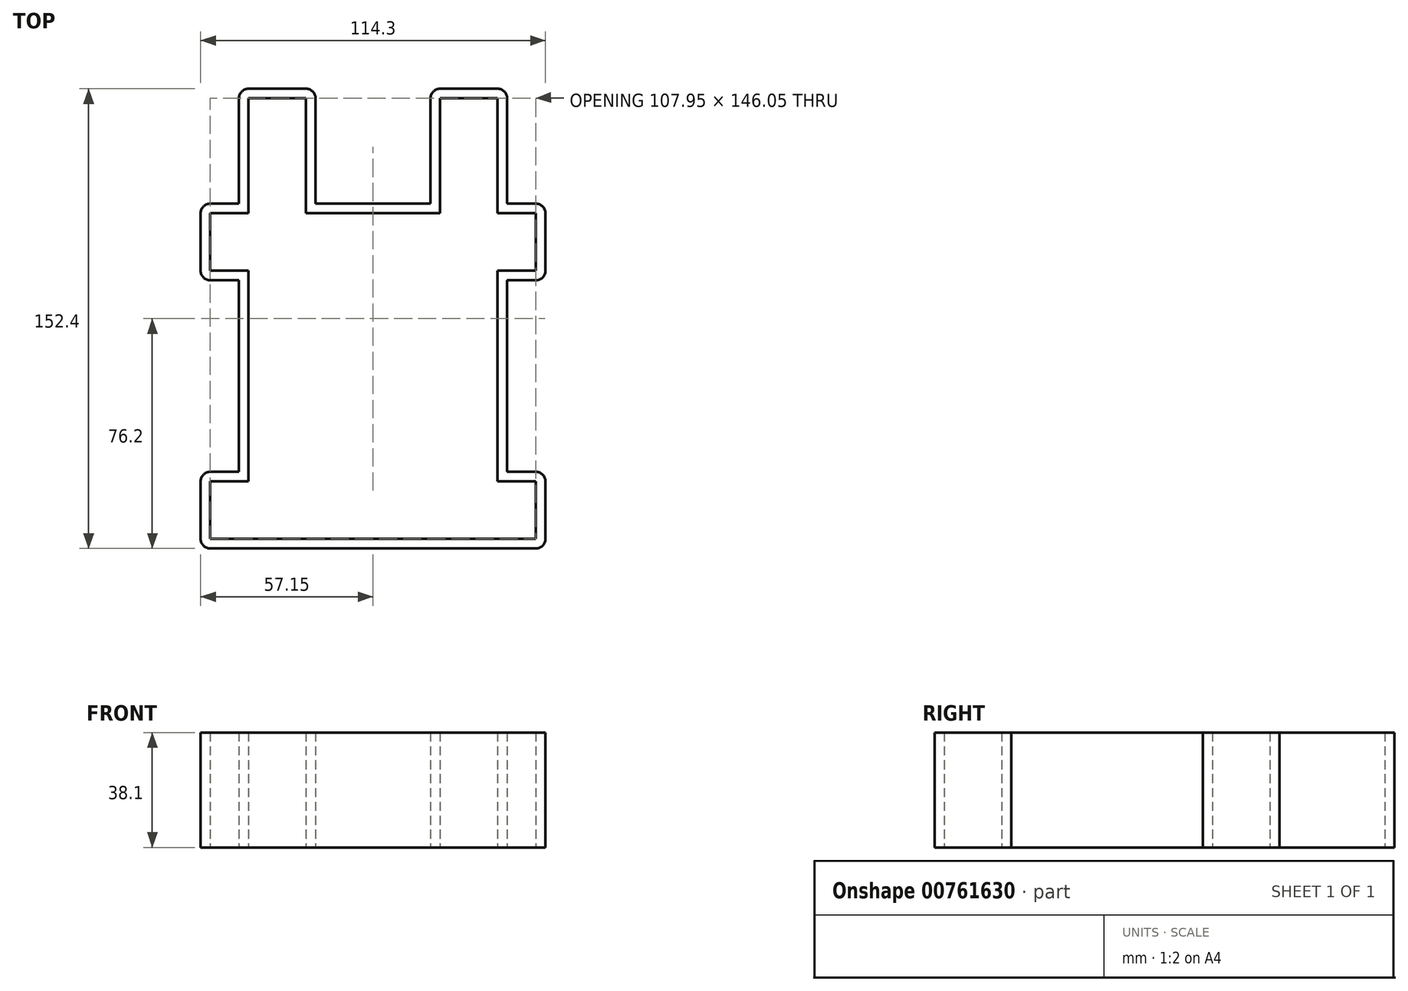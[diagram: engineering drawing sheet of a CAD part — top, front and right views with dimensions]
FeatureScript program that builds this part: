
annotation { "Feature Type Name" : "Feature", "Feature Type Description" : "" }
export const myFeature = defineFeature(function(context is Context, id is Id, definition is map)
    precondition{}
    {
        {
            var Q0;
            Q0=qCreatedBy(makeId("Top.planeOp"),FACE);
            var sketch = newSketch(context, id + "F0", { "sketchPlane" : qUnion([Q0])});
            skLineSegment(sketch, "E0", {"start": v(0, 0) * mm, "end": v(0, -63.5) * mm});
            skLineSegment(sketch, "E1", {"start": v(0, -63.5) * mm, "end": v(-12.7, -63.5) * mm});
            skLineSegment(sketch, "E2", {"start": v(-12.7, -63.5) * mm, "end": v(-12.7, -88.9) * mm});
            skLineSegment(sketch, "E3", {"start": v(-12.7, -88.9) * mm, "end": v(101.6, -88.9) * mm});
            skLineSegment(sketch, "E4", {"start": v(101.6, -88.9) * mm, "end": v(101.6, -63.5) * mm});
            skLineSegment(sketch, "E5", {"start": v(101.6, -63.5) * mm, "end": v(88.9, -63.5) * mm});
            skLineSegment(sketch, "E6", {"start": v(88.9, -63.5) * mm, "end": v(88.9, 0) * mm});
            skLineSegment(sketch, "E7", {"start": v(88.9, 0) * mm, "end": v(101.6, 0) * mm});
            skLineSegment(sketch, "E8", {"start": v(101.6, 0) * mm, "end": v(101.6, 25.4) * mm});
            skLineSegment(sketch, "E9", {"start": v(101.6, 25.4) * mm, "end": v(88.9, 25.4) * mm});
            skLineSegment(sketch, "E10", {"start": v(88.9, 25.4) * mm, "end": v(88.9, 63.5) * mm});
            skLineSegment(sketch, "E11", {"start": v(88.9, 63.5) * mm, "end": v(63.5, 63.5) * mm});
            skLineSegment(sketch, "E12", {"start": v(63.5, 63.5) * mm, "end": v(63.5, 25.4) * mm});
            skLineSegment(sketch, "E13", {"start": v(63.5, 25.4) * mm, "end": v(25.4, 25.4) * mm});
            skLineSegment(sketch, "E14", {"start": v(25.4, 25.4) * mm, "end": v(25.4, 63.5) * mm});
            skLineSegment(sketch, "E15", {"start": v(25.4, 63.5) * mm, "end": v(0, 63.5) * mm});
            skLineSegment(sketch, "E16", {"start": v(0, 63.5) * mm, "end": v(0, 25.4) * mm});
            skLineSegment(sketch, "E17", {"start": v(0, 25.4) * mm, "end": v(-12.7, 25.4) * mm});
            skLineSegment(sketch, "E18", {"start": v(-12.7, 25.4) * mm, "end": v(-12.7, 0) * mm});
            skLineSegment(sketch, "E19", {"start": v(-12.7, 0) * mm, "end": v(0, 0) * mm});
            skLineSegment(sketch, "E20.0", {"start": v(22.22, 22.22) * mm, "end": v(22.22, 60.33) * mm});
            skLineSegment(sketch, "E20.1", {"start": v(66.67, 22.23) * mm, "end": v(22.22, 22.22) * mm});
            skLineSegment(sketch, "E20.2", {"start": v(66.67, 60.33) * mm, "end": v(66.67, 22.23) * mm});
            skLineSegment(sketch, "E20.3", {"start": v(85.72, 60.33) * mm, "end": v(66.67, 60.33) * mm});
            skLineSegment(sketch, "E20.4", {"start": v(85.72, 22.23) * mm, "end": v(85.72, 60.33) * mm});
            skLineSegment(sketch, "E20.5", {"start": v(22.22, 60.33) * mm, "end": v(3.17, 60.33) * mm});
            skLineSegment(sketch, "E20.6", {"start": v(98.42, 22.23) * mm, "end": v(85.72, 22.23) * mm});
            skLineSegment(sketch, "E20.7", {"start": v(98.42, 3.17) * mm, "end": v(98.42, 22.23) * mm});
            skLineSegment(sketch, "E20.8", {"start": v(85.73, 3.17) * mm, "end": v(98.42, 3.17) * mm});
            skLineSegment(sketch, "E20.9", {"start": v(85.73, -66.67) * mm, "end": v(85.73, 3.17) * mm});
            skLineSegment(sketch, "E20.10", {"start": v(-9.53, 3.17) * mm, "end": v(3.17, 3.17) * mm});
            skLineSegment(sketch, "E20.11", {"start": v(-9.53, 22.23) * mm, "end": v(-9.53, 3.17) * mm});
            skLineSegment(sketch, "E20.12", {"start": v(3.17, 22.23) * mm, "end": v(-9.53, 22.23) * mm});
            skLineSegment(sketch, "E20.13", {"start": v(3.17, 60.33) * mm, "end": v(3.17, 22.23) * mm});
            skLineSegment(sketch, "E20.14", {"start": v(3.17, 3.17) * mm, "end": v(3.18, -66.67) * mm});
            skLineSegment(sketch, "E20.15", {"start": v(3.18, -66.67) * mm, "end": v(-9.52, -66.67) * mm});
            skLineSegment(sketch, "E20.16", {"start": v(-9.52, -66.67) * mm, "end": v(-9.52, -85.72) * mm});
            skLineSegment(sketch, "E20.17", {"start": v(-9.52, -85.72) * mm, "end": v(98.43, -85.72) * mm});
            skLineSegment(sketch, "E20.18", {"start": v(98.43, -85.72) * mm, "end": v(98.43, -66.67) * mm});
            skLineSegment(sketch, "E20.19", {"start": v(98.43, -66.67) * mm, "end": v(85.73, -66.67) * mm});
            skSolve(sketch);
        }
        {
            var Q0;
            Q0=makeQuery(id+"F0.imprint","IMPRINT",FACE,{"disambiguationData":[TD([[makeQuery(id+"F0.imprint","IMPRINT",EDGE,{"derivedFrom":sQuery(id+"F0.wireOp",EDGE,"E0")}),1.0]])]});
            extrude(context, id + "F1", {"entities" : qUnion([Q0]), "depth" : 38.1 * mm, "offsetDistance" : 25.4 * mm});
        }
        {
            var Q0;
            Q0=makeQuery(id+"F1.opExtrude","SWEPT_EDGE",EDGE,{"disambiguationData":[OSD([sQuery(id+"F0.wireOp",EDGE,"E15"),sQuery(id+"F0.wireOp",EDGE,"E16")])]});
            var Q1;
            Q1=makeQuery(id+"F1.opExtrude","SWEPT_EDGE",EDGE,{"disambiguationData":[OSD([sQuery(id+"F0.wireOp",EDGE,"E14"),sQuery(id+"F0.wireOp",EDGE,"E15")])]});
            var Q2;
            Q2=makeQuery(id+"F1.opExtrude","SWEPT_EDGE",EDGE,{"disambiguationData":[OSD([sQuery(id+"F0.wireOp",EDGE,"E11"),sQuery(id+"F0.wireOp",EDGE,"E12")])]});
            var Q3;
            Q3=makeQuery(id+"F1.opExtrude","SWEPT_EDGE",EDGE,{"disambiguationData":[OSD([sQuery(id+"F0.wireOp",EDGE,"E10"),sQuery(id+"F0.wireOp",EDGE,"E11")])]});
            var Q4;
            Q4=makeQuery(id+"F1.opExtrude","SWEPT_EDGE",EDGE,{"disambiguationData":[OSD([sQuery(id+"F0.wireOp",EDGE,"E8"),sQuery(id+"F0.wireOp",EDGE,"E9")])]});
            var Q5;
            Q5=makeQuery(id+"F1.opExtrude","SWEPT_EDGE",EDGE,{"disambiguationData":[OSD([sQuery(id+"F0.wireOp",EDGE,"E7"),sQuery(id+"F0.wireOp",EDGE,"E8")])]});
            var Q6;
            Q6=makeQuery(id+"F1.opExtrude","SWEPT_EDGE",EDGE,{"disambiguationData":[OSD([sQuery(id+"F0.wireOp",EDGE,"E4"),sQuery(id+"F0.wireOp",EDGE,"E5")])]});
            var Q7;
            Q7=makeQuery(id+"F1.opExtrude","SWEPT_EDGE",EDGE,{"disambiguationData":[OSD([sQuery(id+"F0.wireOp",EDGE,"E3"),sQuery(id+"F0.wireOp",EDGE,"E4")])]});
            var Q8;
            Q8=makeQuery(id+"F1.opExtrude","SWEPT_EDGE",EDGE,{"disambiguationData":[OSD([sQuery(id+"F0.wireOp",EDGE,"E17"),sQuery(id+"F0.wireOp",EDGE,"E18")])]});
            var Q9;
            Q9=makeQuery(id+"F1.opExtrude","SWEPT_EDGE",EDGE,{"disambiguationData":[OSD([sQuery(id+"F0.wireOp",EDGE,"E18"),sQuery(id+"F0.wireOp",EDGE,"E19")])]});
            var Q10;
            Q10=makeQuery(id+"F1.opExtrude","SWEPT_EDGE",EDGE,{"disambiguationData":[OSD([sQuery(id+"F0.wireOp",EDGE,"E1"),sQuery(id+"F0.wireOp",EDGE,"E2")])]});
            var Q11;
            Q11=makeQuery(id+"F1.opExtrude","SWEPT_EDGE",EDGE,{"disambiguationData":[OSD([sQuery(id+"F0.wireOp",EDGE,"E2"),sQuery(id+"F0.wireOp",EDGE,"E3")])]});
            fillet(context, id + "F2", {"entities" : qUnion([Q0, Q1, Q2, Q3, Q4, Q5, Q6, Q7, Q8, Q9, Q10, Q11]), "radius" : 3.17 * mm, "tangentPropagation" : true, "allowEdgeOverflow" : false});
        }
    });
